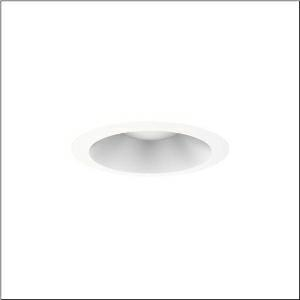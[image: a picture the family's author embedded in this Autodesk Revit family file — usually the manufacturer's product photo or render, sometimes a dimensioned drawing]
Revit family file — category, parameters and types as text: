
# Revit family: lunis_31_midi_51dn16dg32
name_source: partatom
category: Lighting Fixtures
units: mm (PartAtom-declared; Revit-internal decimal feet)

## family parameters
Cut with Voids When Loaded = No
Host = Face
Light Source = No
Part Type = Normal
Room Calculation Point = No
Round Connector Dimension = Use Diameter
Shared = No

## types (1)
- Lunis 31 midi (1 x LED, 2000 lm, 17 W, 3000K)
    Apparent Load = 17 VA
    CIE Flux Codes = 64 93 99 100 100
    Color Rendering = 80
    Color Temperature = 3000K
    Default Elevation = 1800 mm
    Description = Lunis 31,  midi, downlight, light control with reflector, light emission: direct distribution, LED rated luminous flux: 2.050lm, light colour: 830, control gear: ECG DALI, mains connection: 220..240V, AC, 50/60Hz, housing, white, protection rating (complete): IP20, insulation class (complete): insulation class II (safety insulation), certification: CE, packaging unit: 1 piece
    Height = 0 mm  [stored 0 ft]
    Lamp = 1 x LED
    Lamp Light Flux = 2000 lm
    Lamp Power = 17 W
    Lamp count = 1
    Length = 259 mm
    Luminous efficacy = 118 lm/W
    Manufacturer = Siteco
    ModVariant = No
    Model = 51DN16DG32
    Mounting Place = Ceiling
    Mounting Type = Recessed
    Number of Poles = 1
    OnlyDefault = Yes
    Power Factor = 1
    Product Name = Lunis 31 midi
    Product group = downlight | ceiling recessed
    ProductGroupID = 402
    Protection Class = Protection class II
    Protection Degree = IP 20
    RLX_Detail_Level = 1
    RlxData = <blob elided: 23673 chars, md5=43438b9a>
    Socket = socket
    Standby Power = 0 W
    System Light Flux = 2000 lm
    System Power = 17 W
    Type Comments = Product without accessories
    Type Image = l_1006711.jpg
    URL = http://relux.com
    VarID = ---
    Voltage = 0 V
    Weight = 0.00 kg
    Width = 0 mm  [stored 0 ft]

note: [stored X ft] marks values corroborated as IEEE doubles in the binary element streams (Revit-internal decimal feet)

## geometry (parser evidence)
native form markers: Blend x4, Sweep x11
no freeform markers — native parametric forms only
